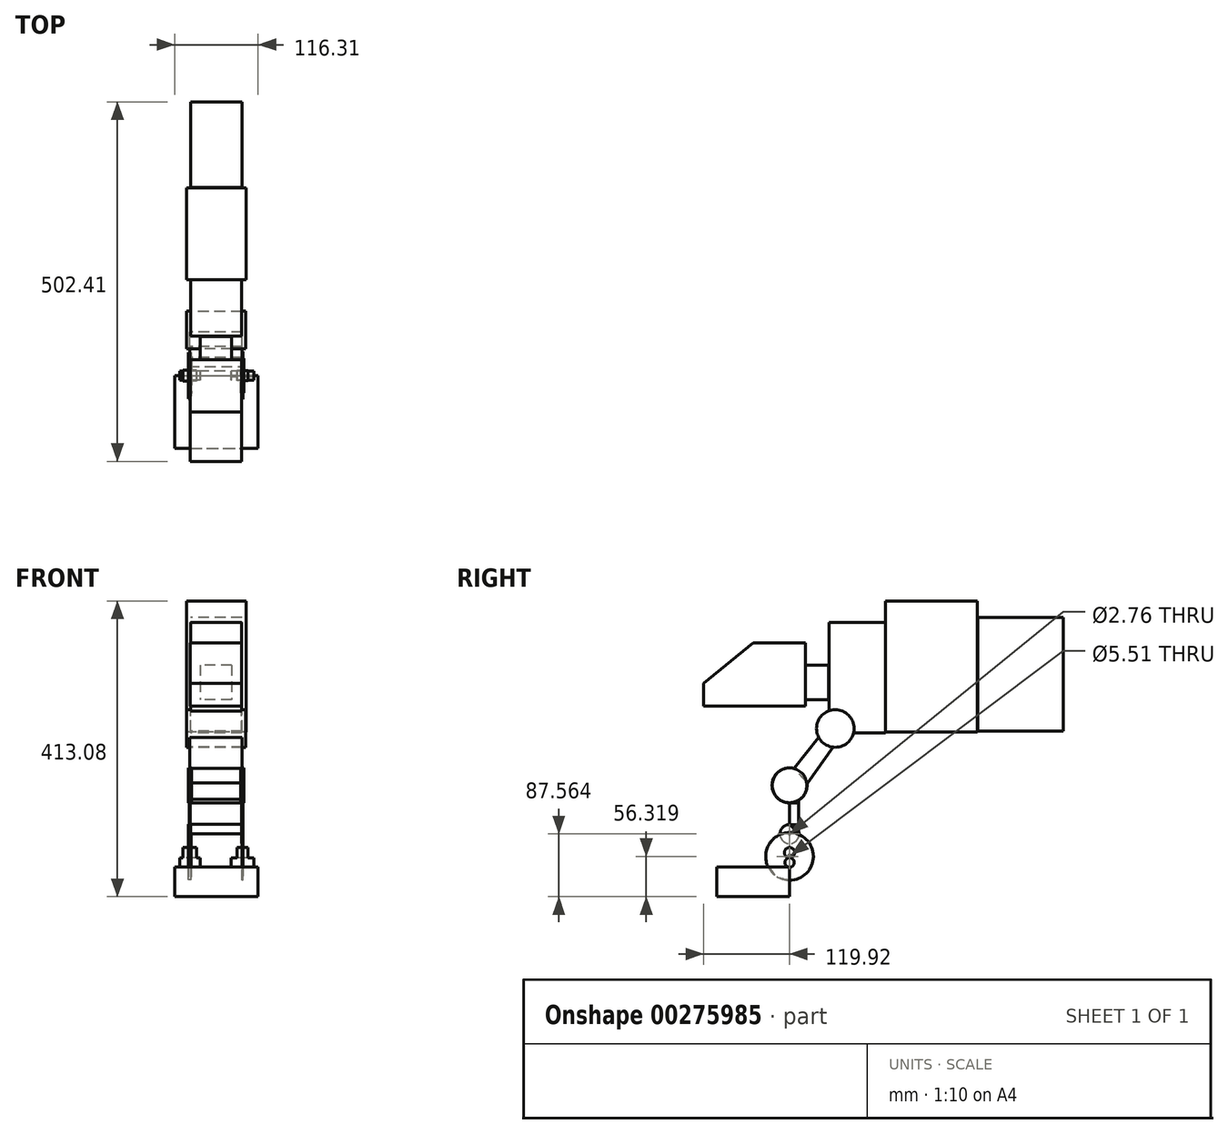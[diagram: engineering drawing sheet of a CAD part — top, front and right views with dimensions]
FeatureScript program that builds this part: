
annotation { "Feature Type Name" : "Feature", "Feature Type Description" : "" }
export const myFeature = defineFeature(function(context is Context, id is Id, definition is map)
    precondition{}
    {
        {
            var Q0;
            Q0=qCreatedBy(makeId("Front.planeOp"),FACE);
            var sketch = newSketch(context, id + "F0", { "sketchPlane" : qUnion([Q0])});
            skLineSegment(sketch, "E0.bottom", {"start": v(-54.15, -26.59) * mm, "end": v(62.16, -26.59) * mm});
            skLineSegment(sketch, "E0.top", {"start": v(-54.15, -68.11) * mm, "end": v(62.16, -68.11) * mm});
            skLineSegment(sketch, "E0.left", {"start": v(-54.15, -26.59) * mm, "end": v(-54.15, -68.11) * mm});
            skLineSegment(sketch, "E0.right", {"start": v(62.16, -26.59) * mm, "end": v(62.16, -68.11) * mm});
            skSolve(sketch);
        }
        {
            var Q0;
            Q0 = qSketchRegion(id + "F0", true);
            extrude(context, id + "F1", {"entities" : qUnion([Q0]), "depth" : 101.85 * mm});
        }
        {
            var Q0;
            Q0=qCreatedBy(makeId("Front.planeOp"),FACE);
            var sketch = newSketch(context, id + "F2", { "sketchPlane" : qUnion([Q0])});
            skLineSegment(sketch, "E1.bottom", {"start": v(-47.3, -26.59) * mm, "end": v(-18.9, -26.59) * mm});
            skLineSegment(sketch, "E1.top", {"start": v(-47.3, -20.28) * mm, "end": v(-18.9, -20.28) * mm});
            skLineSegment(sketch, "E1.left", {"start": v(-47.3, -26.59) * mm, "end": v(-47.3, -20.28) * mm});
            skLineSegment(sketch, "E1.right", {"start": v(-18.9, -26.59) * mm, "end": v(-18.9, -20.28) * mm});
            skLineSegment(sketch, "E2.bottom", {"start": v(24.32, -26.83) * mm, "end": v(56.13, -26.83) * mm});
            skLineSegment(sketch, "E2.top", {"start": v(24.32, -20.28) * mm, "end": v(56.13, -20.28) * mm});
            skLineSegment(sketch, "E2.left", {"start": v(24.32, -26.83) * mm, "end": v(24.32, -20.28) * mm});
            skLineSegment(sketch, "E2.right", {"start": v(56.13, -26.83) * mm, "end": v(56.13, -20.28) * mm});
            skSolve(sketch);
        }
        {
            var Q0;
            Q0=makeQuery(id+"F2.imprint","IMPRINT",FACE,{"disambiguationData":[TD([[makeQuery(id+"F2.imprint","IMPRINT",EDGE,{"derivedFrom":sQuery(id+"F2.wireOp",EDGE,"E2.bottom")}),1.0]])]});
            var Q1;
            Q1=makeQuery(id+"F2.imprint","IMPRINT",FACE,{"disambiguationData":[TD([[makeQuery(id+"F2.imprint","IMPRINT",EDGE,{"derivedFrom":sQuery(id+"F2.wireOp",EDGE,"E1.bottom")}),1.0]])]});
            var Q2;
            Q2=sQuery(id+"F2.wireOp",EDGE,"E1.top");
            revolve(context, id + "F3", {"operationType" : NewBodyOperationType.ADD, "entities" : qUnion([Q0, Q1]), "axis" : qUnion([Q2]), "revolveType" : RevolveType.FULL});
        }
        {
            var Q0;
            Q0=qCreatedBy(makeId("Front.planeOp"),FACE);
            var sketch = newSketch(context, id + "F4", { "sketchPlane" : qUnion([Q0])});
            skLineSegment(sketch, "E3.bottom", {"start": v(-42.7, -14.02) * mm, "end": v(-23.74, -14.02) * mm});
            skLineSegment(sketch, "E3.top", {"start": v(-42.7, -6.57) * mm, "end": v(-23.74, -6.57) * mm});
            skLineSegment(sketch, "E3.left", {"start": v(-42.7, -14.02) * mm, "end": v(-42.7, -6.57) * mm});
            skLineSegment(sketch, "E3.right", {"start": v(-23.74, -14.02) * mm, "end": v(-23.74, -6.57) * mm});
            skLineSegment(sketch, "E4.bottom", {"start": v(32.94, -13.8) * mm, "end": v(47.84, -13.8) * mm});
            skLineSegment(sketch, "E4.top", {"start": v(32.94, -6.57) * mm, "end": v(47.84, -6.57) * mm});
            skLineSegment(sketch, "E4.left", {"start": v(32.94, -13.8) * mm, "end": v(32.94, -6.57) * mm});
            skLineSegment(sketch, "E4.right", {"start": v(47.84, -13.8) * mm, "end": v(47.84, -6.57) * mm});
            skSolve(sketch);
        }
        {
            var Q0;
            Q0 = qSketchRegion(id + "F4", true);
            var Q1;
            Q1=sQuery(id+"F4.wireOp",EDGE,"E3.top");
            revolve(context, id + "F5", {"entities" : qUnion([Q0]), "axis" : qUnion([Q1]), "revolveType" : RevolveType.FULL});
        }
        {
            var Q0;
            Q0=qCreatedBy(makeId("Front.planeOp"),FACE);
            var sketch = newSketch(context, id + "F6", { "sketchPlane" : qUnion([Q0])});
            skLineSegment(sketch, "E5.bottom", {"start": v(-35.12, -9.03) * mm, "end": v(-31.44, -9.03) * mm});
            skLineSegment(sketch, "E5.top", {"start": v(-35.12, 20.6) * mm, "end": v(-31.44, 20.6) * mm});
            skLineSegment(sketch, "E5.left", {"start": v(-35.12, -9.03) * mm, "end": v(-35.12, 20.6) * mm});
            skLineSegment(sketch, "E5.right", {"start": v(-31.44, -9.03) * mm, "end": v(-31.44, 20.6) * mm});
            skLineSegment(sketch, "E6.bottom", {"start": v(39.55, -11.8) * mm, "end": v(41.16, -11.8) * mm});
            skLineSegment(sketch, "E6.top", {"start": v(39.55, 21.52) * mm, "end": v(41.16, 21.52) * mm});
            skLineSegment(sketch, "E6.left", {"start": v(39.55, -11.8) * mm, "end": v(39.55, 21.52) * mm});
            skLineSegment(sketch, "E6.right", {"start": v(41.16, -11.8) * mm, "end": v(41.16, 21.52) * mm});
            skSolve(sketch);
        }
        {
            var Q0;
            Q0 = qSketchRegion(id + "F6", true);
            var Q1;
            Q1=sQuery(id+"F6.wireOp",EDGE,"E6.bottom");
            revolve(context, id + "F7", {"entities" : qUnion([Q0]), "axis" : qUnion([Q1]), "revolveType" : RevolveType.FULL});
        }
        {
            var Q0;
            Q0=qCreatedBy(makeId("Front.planeOp"),FACE);
            var sketch = newSketch(context, id + "F8", { "sketchPlane" : qUnion([Q0])});
            skLineSegment(sketch, "E7.bottom", {"start": v(-34.66, 19.45) * mm, "end": v(-31.9, 19.45) * mm});
            skLineSegment(sketch, "E7.top", {"start": v(-34.66, 32.78) * mm, "end": v(-31.9, 32.78) * mm});
            skLineSegment(sketch, "E7.left", {"start": v(-34.66, 19.45) * mm, "end": v(-34.66, 32.78) * mm});
            skLineSegment(sketch, "E7.right", {"start": v(-31.9, 19.45) * mm, "end": v(-31.9, 32.78) * mm});
            skLineSegment(sketch, "E8.bottom", {"start": v(39.32, 20.83) * mm, "end": v(40.47, 20.83) * mm});
            skLineSegment(sketch, "E8.top", {"start": v(39.32, 32.78) * mm, "end": v(40.47, 32.78) * mm});
            skLineSegment(sketch, "E8.left", {"start": v(39.32, 20.83) * mm, "end": v(39.32, 32.78) * mm});
            skLineSegment(sketch, "E8.right", {"start": v(40.47, 20.83) * mm, "end": v(40.47, 32.78) * mm});
            skSolve(sketch);
        }
        {
            var Q0;
            Q0 = qSketchRegion(id + "F8", true);
            var Q1;
            Q1=sQuery(id+"F8.wireOp",EDGE,"E7.bottom");
            revolve(context, id + "F9", {"entities" : qUnion([Q0]), "axis" : qUnion([Q1]), "revolveType" : RevolveType.FULL});
        }
        {
            var Q0;
            Q0=qCreatedBy(makeId("Front.planeOp"),FACE);
            var sketch = newSketch(context, id + "F10", { "sketchPlane" : qUnion([Q0])});
            skLineSegment(sketch, "E9.bottom", {"start": v(-34.2, 33.24) * mm, "end": v(-32.59, 33.24) * mm});
            skLineSegment(sketch, "E9.top", {"start": v(-34.2, 62.65) * mm, "end": v(-32.59, 62.65) * mm});
            skLineSegment(sketch, "E9.left", {"start": v(-34.2, 33.24) * mm, "end": v(-34.2, 62.65) * mm});
            skLineSegment(sketch, "E9.right", {"start": v(-32.59, 33.24) * mm, "end": v(-32.59, 62.65) * mm});
            skLineSegment(sketch, "E10.bottom", {"start": v(39.1, 32.78) * mm, "end": v(40.7, 32.78) * mm});
            skLineSegment(sketch, "E10.top", {"start": v(39.1, 62.65) * mm, "end": v(40.7, 62.65) * mm});
            skLineSegment(sketch, "E10.left", {"start": v(39.1, 32.78) * mm, "end": v(39.1, 62.65) * mm});
            skLineSegment(sketch, "E10.right", {"start": v(40.7, 32.78) * mm, "end": v(40.7, 62.65) * mm});
            skSolve(sketch);
        }
        {
            var Q0;
            Q0 = qSketchRegion(id + "F10", true);
            extrude(context, id + "F11", {"entities" : qUnion([Q0]), "oppositeDirection" : true, "depth" : 12.45 * mm});
        }
        {
            var Q0;
            Q0=qCreatedBy(makeId("Front.planeOp"),FACE);
            var sketch = newSketch(context, id + "F12", { "sketchPlane" : qUnion([Q0])});
            skLineSegment(sketch, "E11.bottom", {"start": v(-35.3, 62.92) * mm, "end": v(-30.71, 62.92) * mm});
            skLineSegment(sketch, "E11.top", {"start": v(-35.3, 87.43) * mm, "end": v(-30.71, 87.43) * mm});
            skLineSegment(sketch, "E11.left", {"start": v(-35.3, 62.92) * mm, "end": v(-35.3, 87.43) * mm});
            skLineSegment(sketch, "E11.right", {"start": v(-30.71, 62.92) * mm, "end": v(-30.71, 87.43) * mm});
            skLineSegment(sketch, "E12.bottom", {"start": v(37.69, 63.2) * mm, "end": v(42.27, 63.2) * mm});
            skLineSegment(sketch, "E12.top", {"start": v(37.69, 87.43) * mm, "end": v(42.27, 87.43) * mm});
            skLineSegment(sketch, "E12.left", {"start": v(37.69, 63.2) * mm, "end": v(37.69, 87.43) * mm});
            skLineSegment(sketch, "E12.right", {"start": v(42.27, 63.2) * mm, "end": v(42.27, 87.43) * mm});
            skSolve(sketch);
        }
        {
            var Q0;
            Q0 = qSketchRegion(id + "F12", true);
            var Q1;
            Q1=sQuery(id+"F12.wireOp",EDGE,"E11.top");
            revolve(context, id + "F13", {"entities" : qUnion([Q0]), "axis" : qUnion([Q1]), "revolveType" : RevolveType.FULL});
        }
        {
            var Q0;
            Q0=qCreatedBy(makeId("Right.planeOp"),FACE);
            var sketch = newSketch(context, id + "F14", { "sketchPlane" : qUnion([Q0])});
            skLineSegment(sketch, "E13", {"start": v(0, 33.3) * mm, "end": v(12.58, 33.3) * mm});
            skLineSegment(sketch, "E14", {"start": v(12.58, 33.3) * mm, "end": v(12.58, 19.3) * mm});
            skLineSegment(sketch, "E15", {"start": v(12.7, 19.4) * mm, "end": v(0, 33.3) * mm});
            skLineSegment(sketch, "E16", {"start": v(0, 62.75) * mm, "end": v(12.58, 62.75) * mm});
            skLineSegment(sketch, "E17", {"start": v(12.58, 62.75) * mm, "end": v(12.58, 67.82) * mm});
            skLineSegment(sketch, "E18", {"start": v(12.82, 67.82) * mm, "end": v(0, 62.75) * mm});
            skSolve(sketch);
        }
        {
            var Q0;
            Q0 = qSketchRegion(id + "F14", true);
            extrude(context, id + "F15", {"entities" : qUnion([Q0]), "oppositeDirection" : true, "depth" : 35.05 * mm, "hasSecondDirection" : true, "secondDirectionOppositeDirection" : false, "secondDirectionDepth" : 40.64 * mm});
        }
        {
            var Q0;
            Q0=qCreatedBy(makeId("Right.planeOp"),FACE);
            var sketch = newSketch(context, id + "F16", { "sketchPlane" : qUnion([Q0])});
            skLineSegment(sketch, "E19", {"start": v(6.17, 111.45) * mm, "end": v(56.34, 174.3) * mm});
            skLineSegment(sketch, "E20", {"start": v(6.17, 111.45) * mm, "end": v(25.2, 90.7) * mm});
            skLineSegment(sketch, "E21", {"start": v(25.2, 90.7) * mm, "end": v(73.63, 158.15) * mm});
            skLineSegment(sketch, "E22", {"start": v(73.63, 158.15) * mm, "end": v(56.34, 174.3) * mm});
            skSolve(sketch);
        }
        {
            var Q0;
            Q0 = qSketchRegion(id + "F16", true);
            extrude(context, id + "F17", {"entities" : qUnion([Q0]), "operationType" : NewBodyOperationType.ADD, "depth" : 39.88 * mm, "hasSecondDirection" : true, "secondDirectionOppositeDirection" : true, "secondDirectionDepth" : 33.53 * mm});
        }
        {
            var Q0;
            Q0=qCreatedBy(makeId("Right.planeOp"),FACE);
            var sketch = newSketch(context, id + "F18", { "sketchPlane" : qUnion([Q0])});
            skCircle(sketch, "E23", {"center": v(63.83, 166.8) * mm, "radius": 26.2 * mm});
            skSolve(sketch);
        }
        {
            var Q0;
            Q0 = qSketchRegion(id + "F18", true);
            extrude(context, id + "F19", {"entities" : qUnion([Q0]), "operationType" : NewBodyOperationType.ADD, "depth" : 44.96 * mm, "hasSecondDirection" : true, "secondDirectionOppositeDirection" : true, "secondDirectionDepth" : 37.6 * mm});
        }
        {
            var Q0;
            Q0=qCreatedBy(makeId("Right.planeOp"),FACE);
            var sketch = newSketch(context, id + "F20", { "sketchPlane" : qUnion([Q0])});
            skLineSegment(sketch, "E24.bottom", {"start": v(55.04, 161.04) * mm, "end": v(134.03, 161.04) * mm});
            skLineSegment(sketch, "E24.top", {"start": v(55.04, 314.99) * mm, "end": v(134.03, 314.99) * mm});
            skLineSegment(sketch, "E24.left", {"start": v(55.04, 161.04) * mm, "end": v(55.04, 314.99) * mm});
            skLineSegment(sketch, "E24.right", {"start": v(134.03, 161.04) * mm, "end": v(134.03, 314.99) * mm});
            skSolve(sketch);
        }
        {
            var Q0;
            Q0 = qSketchRegion(id + "F20", true);
            extrude(context, id + "F21", {"entities" : qUnion([Q0]), "operationType" : NewBodyOperationType.ADD, "depth" : 39.12 * mm, "hasSecondDirection" : true, "secondDirectionOppositeDirection" : true, "secondDirectionDepth" : 32.26 * mm});
        }
        {
            var Q0;
            Q0=qCreatedBy(makeId("Right.planeOp"),FACE);
            var sketch = newSketch(context, id + "F22", { "sketchPlane" : qUnion([Q0])});
            skLineSegment(sketch, "E25.bottom", {"start": v(134.03, 162.2) * mm, "end": v(262.04, 162.2) * mm});
            skLineSegment(sketch, "E25.top", {"start": v(134.03, 344.97) * mm, "end": v(262.04, 344.97) * mm});
            skLineSegment(sketch, "E25.left", {"start": v(134.03, 162.2) * mm, "end": v(134.03, 344.97) * mm});
            skLineSegment(sketch, "E25.right", {"start": v(262.04, 162.2) * mm, "end": v(262.04, 344.97) * mm});
            skSolve(sketch);
        }
        {
            var Q0;
            Q0 = qSketchRegion(id + "F22", true);
            extrude(context, id + "F23", {"entities" : qUnion([Q0]), "operationType" : NewBodyOperationType.ADD, "depth" : 45.47 * mm, "hasSecondDirection" : true, "secondDirectionOppositeDirection" : true, "secondDirectionDepth" : 38.1 * mm});
        }
        {
            var Q0;
            Q0=qCreatedBy(makeId("Right.planeOp"),FACE);
            var sketch = newSketch(context, id + "F24", { "sketchPlane" : qUnion([Q0])});
            skLineSegment(sketch, "E26.bottom", {"start": v(263.13, 163.34) * mm, "end": v(382.49, 163.34) * mm});
            skLineSegment(sketch, "E26.top", {"start": v(263.13, 321.9) * mm, "end": v(382.49, 321.9) * mm});
            skLineSegment(sketch, "E26.left", {"start": v(263.13, 163.34) * mm, "end": v(263.13, 321.9) * mm});
            skLineSegment(sketch, "E26.right", {"start": v(382.49, 163.34) * mm, "end": v(382.49, 321.9) * mm});
            skSolve(sketch);
        }
        {
            var Q0;
            Q0 = qSketchRegion(id + "F24", true);
            extrude(context, id + "F25", {"entities" : qUnion([Q0]), "depth" : 39.62 * mm, "hasSecondDirection" : true, "secondDirectionOppositeDirection" : true, "secondDirectionDepth" : 32.26 * mm});
        }
        {
            var Q0;
            Q0=qCreatedBy(makeId("Right.planeOp"),FACE);
            var sketch = newSketch(context, id + "F26", { "sketchPlane" : qUnion([Q0])});
            skLineSegment(sketch, "E27.bottom", {"start": v(54.6, 255.6) * mm, "end": v(21.15, 255.6) * mm});
            skLineSegment(sketch, "E27.top", {"start": v(54.6, 207.17) * mm, "end": v(21.15, 207.17) * mm});
            skLineSegment(sketch, "E27.left", {"start": v(54.6, 255.6) * mm, "end": v(54.6, 207.17) * mm});
            skLineSegment(sketch, "E27.right", {"start": v(21.15, 255.6) * mm, "end": v(21.15, 207.17) * mm});
            skSolve(sketch);
        }
        {
            var Q0;
            Q0 = qSketchRegion(id + "F26", true);
            extrude(context, id + "F27", {"entities" : qUnion([Q0]), "depth" : 25.4 * mm, "hasSecondDirection" : true, "secondDirectionOppositeDirection" : true, "secondDirectionDepth" : 18.54 * mm});
        }
        {
            var Q0;
            Q0=qCreatedBy(makeId("Right.planeOp"),FACE);
            var sketch = newSketch(context, id + "F28", { "sketchPlane" : qUnion([Q0])});
            skLineSegment(sketch, "E28", {"start": v(21.92, 255.6) * mm, "end": v(21.92, 286.16) * mm});
            skLineSegment(sketch, "E29", {"start": v(21.92, 286.16) * mm, "end": v(-50.73, 286.16) * mm});
            skLineSegment(sketch, "E30", {"start": v(-50.73, 286.16) * mm, "end": v(-119.92, 230.23) * mm});
            skLineSegment(sketch, "E31", {"start": v(-119.92, 230.23) * mm, "end": v(-119.92, 198.52) * mm});
            skLineSegment(sketch, "E32", {"start": v(-119.92, 198.52) * mm, "end": v(21.92, 198.52) * mm});
            skLineSegment(sketch, "E33", {"start": v(21.92, 198.52) * mm, "end": v(21.92, 255.6) * mm});
            skSolve(sketch);
        }
        {
            var Q0;
            Q0 = qSketchRegion(id + "F28", true);
            extrude(context, id + "F29", {"entities" : qUnion([Q0]), "operationType" : NewBodyOperationType.ADD, "depth" : 39.12 * mm, "hasSecondDirection" : true, "secondDirectionOppositeDirection" : true, "secondDirectionDepth" : 33.02 * mm});
        }
    });
